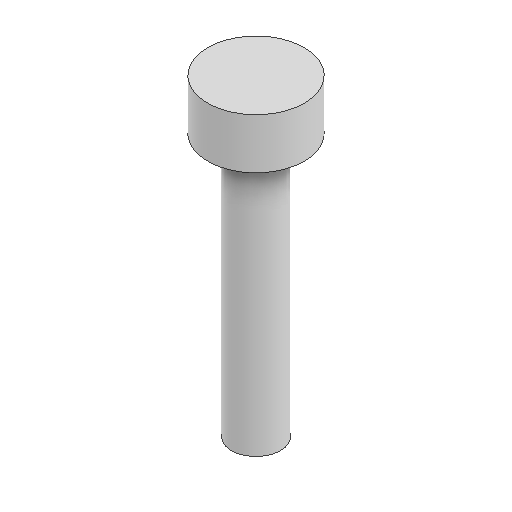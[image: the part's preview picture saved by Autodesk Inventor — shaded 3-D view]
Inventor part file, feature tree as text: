
AUTODESK INVENTOR PART (.ipt)
format: ipt  version: 2025 (Build 290162010, 162A)  size: 88,064 bytes
history: native  units: in
note: dims shown in document units (in); Inventor stores cm internally (conversion verified against a paired STEP export)
features: revolve x1, sketch x1
ambient origin geometry x8: Origin, YZ Plane, XZ Plane, XY Plane, X Axis, Y Axis, Z Axis, Center Point
bodies: Solid1 (feature_tree)
feature tree (2):
  revolve  "Revolution1"  [1 undecoded]
  sketch  "Sketch1"  dims[d1=0.14in d2=0.071in d3=0.073in d4=0.381in d5=90.0deg]
note: 1 required parameter value undecoded (feature->parameter linkage not recoverable at this tier; creation-order binding heuristic only, values carry confidence <= 0.55)
